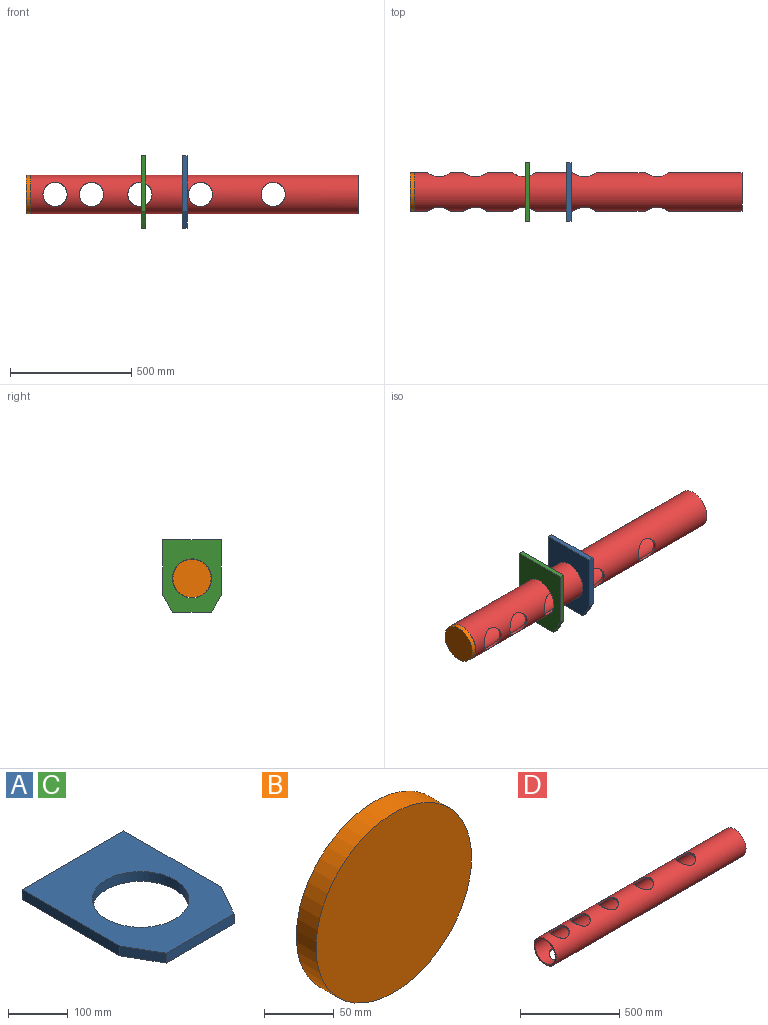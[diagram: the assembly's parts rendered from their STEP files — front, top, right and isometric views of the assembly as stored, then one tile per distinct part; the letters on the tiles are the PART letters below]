
ASSEMBLY  parts=4 mates=3
PART A: 9 faces, bbox 240x300x20 mm
  f0: plane 230x20mm, normal (1,0,0), area 4600mm2, adj f1,f5,f7,f8
  f1: plane 240x20mm, normal (0,1,0), area 4800mm2, adj f0,f2,f7,f8
  f2: plane 230x20mm, normal (-1,0,0), area 4600mm2, adj f1,f3,f7,f8
  f3: plane 70x40mm, normal (-0.87,-0.5,0), area 1612.5mm2, adj f2,f4,f7,f8
  f4: plane 160x20mm, normal (0,-1,0), area 3200mm2, adj f3,f5,f7,f8
  f5: plane 70x40mm, normal (0.87,-0.5,0), area 1612.5mm2, adj f0,f4,f7,f8
  f6: cylinder r=80.5mm len=161mm, axis (0,0,-1), area 10115.9mm2, adj f7,f8
  f7: plane 300x240mm, normal (0,0,1), area 48841.7mm2, adj f0,f1,f2,f3,f4,f5,f6
  f8: plane 300x240mm, normal (0,0,-1), area 48841.7mm2, adj f0,f1,f2,f3,f4,f5,f6
PART B: 3 faces, bbox 158x20x158 mm
  f0: cylinder r=79mm len=158mm, axis (0,1,0), area 9927.4mm2, adj f1,f2
  f1: plane 158x158mm, normal (0,-1,0), area 19606.7mm2, adj f0
  f2: plane 158x158mm, normal (0,1,0), area 19606.7mm2, adj f0
PART C: same geometry as A
PART D: 14 faces, bbox 1350x160x160 mm
  f0: cylinder r=70.5mm len=1350mm, axis (-1,0,0), area 513252mm2, adj f2,f3,f4,f5,f6,f7,f8,f9
  f1: cylinder r=80mm len=1350mm, axis (-1,0,0), area 595514.7mm2, adj f2,f3,f4,f5,f6,f7,f8,f9
  f2: plane 160x160mm, normal (1,0,0), area 4491.7mm2, adj f0,f1
  f3: plane 160x160mm, normal (-1,0,0), area 4491.7mm2, adj f0,f1
  f4: cylinder r=50mm len=100mm, axis (0,0,-1), area 3438mm2, adj f0,f1
  f5: cylinder r=50mm len=100mm, axis (0,0,-1), area 3438.2mm2, adj f0,f1
  f6: cylinder r=50mm len=100mm, axis (0,0,-1), area 3438mm2, adj f0,f1
  f7: cylinder r=50mm len=100mm, axis (0,0,-1), area 3438.2mm2, adj f0,f1
  f8: cylinder r=50mm len=100mm, axis (0,0,-1), area 3438mm2, adj f0,f1
  f9: cylinder r=50mm len=100mm, axis (0,0,-1), area 3438.2mm2, adj f0,f1
  f10: cylinder r=50mm len=100mm, axis (0,0,-1), area 3438mm2, adj f0,f1
  f11: cylinder r=50mm len=100mm, axis (0,0,-1), area 3438.2mm2, adj f0,f1
  f12: cylinder r=50mm len=100mm, axis (0,0,-1), area 3438mm2, adj f0,f1
  f13: cylinder r=50mm len=100mm, axis (0,0,-1), area 3438.2mm2, adj f0,f1
PLACE A rot(axis=(0.58,-0.58,-0.58),120deg) t=(1281.79,194.57,239.43)mm
PLACE B rot(axis=(0.71,0.71,0),180deg) t=(636.79,195.05,210.55)mm
PLACE C rot(axis=(0.58,-0.58,-0.58),120deg) t=(1111.79,194.57,239.43)mm
PLACE D rot(axis=(1,0,0),90deg) t=(636.79,194.57,209.43)mm fixed
MATE fastened C.f6 <-> D.f1  axis (-1,0,0) through (1091.79,194.57,209.43)mm
MATE fastened B.f0 <-> D.f0  axis (1,0,0) through (636.79,194.57,209.43)mm
MATE fastened A.f6 <-> D.f1  axis (-1,0,0) through (1261.79,194.57,209.43)mm
